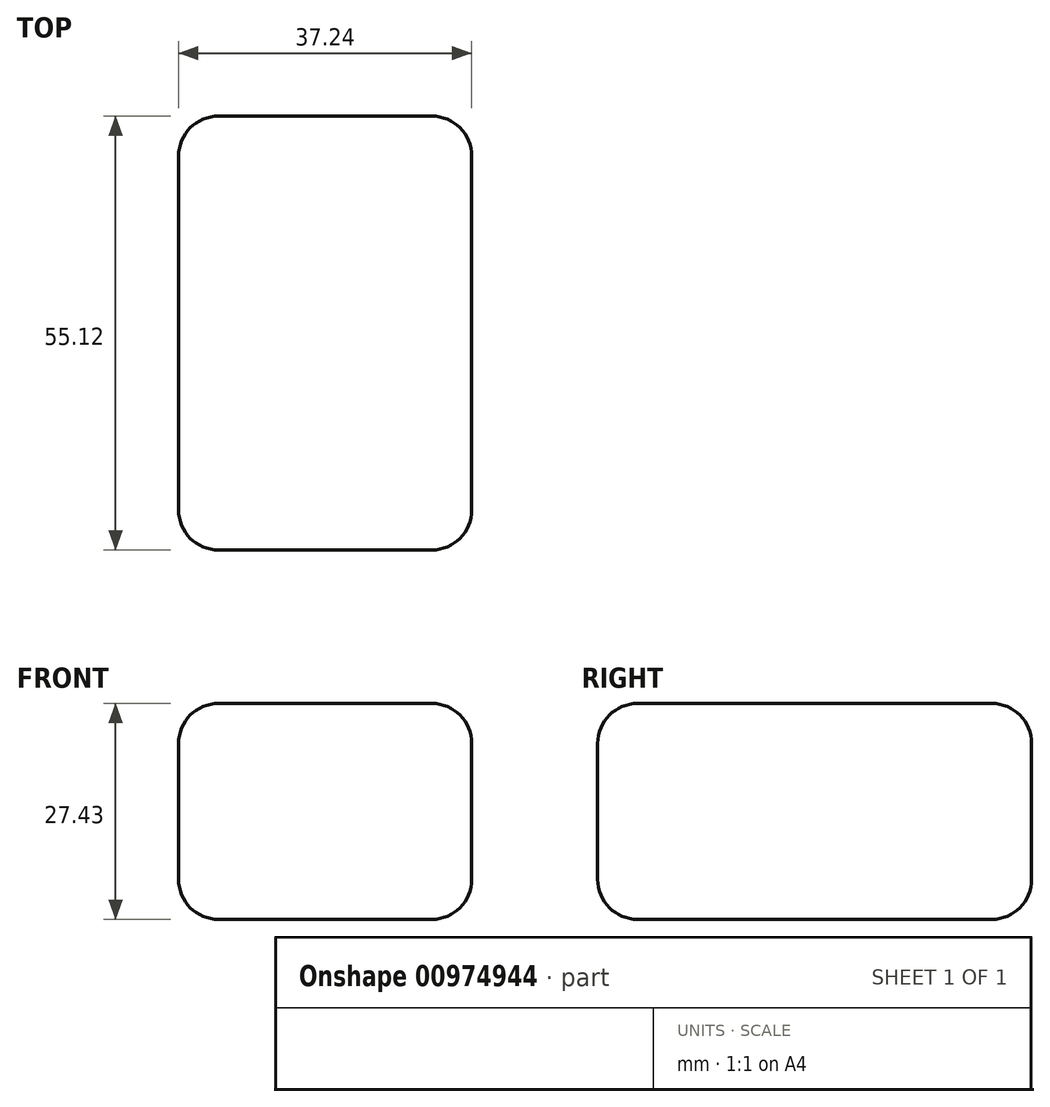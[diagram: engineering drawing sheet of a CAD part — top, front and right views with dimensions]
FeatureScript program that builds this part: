
annotation { "Feature Type Name" : "Feature", "Feature Type Description" : "" }
export const myFeature = defineFeature(function(context is Context, id is Id, definition is map)
    precondition{}
    {
        {
            var Q0;
            Q0=qCreatedBy(makeId("Top.planeOp"),FACE);
            var sketch = newSketch(context, id + "F0", { "sketchPlane" : qUnion([Q0])});
            skLineSegment(sketch, "E0.bottom", {"start": v(-67.38, 58.35) * mm, "end": v(-30.14, 58.35) * mm});
            skLineSegment(sketch, "E0.top", {"start": v(-67.38, 3.23) * mm, "end": v(-30.14, 3.23) * mm});
            skLineSegment(sketch, "E0.left", {"start": v(-67.38, 58.35) * mm, "end": v(-67.38, 3.23) * mm});
            skLineSegment(sketch, "E0.right", {"start": v(-30.14, 58.35) * mm, "end": v(-30.14, 3.23) * mm});
            skSolve(sketch);
        }
        {
            var Q0;
            Q0 = qSketchRegion(id + "F0", true);
            extrude(context, id + "F1", {"entities" : qUnion([Q0]), "depth" : 27.43 * mm, "offsetDistance" : 25.4 * mm});
        }
        {
            var Q0;
            Q0=makeQuery(id+"F1.opExtrude","CAP_EDGE",EDGE,{"disambiguationData":[OSD([sQuery(id+"F0.wireOp",EDGE,"E0.left")])],"isStart":false});
            var Q1;
            Q1=makeQuery(id+"F1.opExtrude","CAP_EDGE",EDGE,{"disambiguationData":[OSD([sQuery(id+"F0.wireOp",EDGE,"E0.right")])],"isStart":false});
            var Q2;
            Q2=makeQuery(id+"F1.opExtrude","CAP_EDGE",EDGE,{"disambiguationData":[OSD([sQuery(id+"F0.wireOp",EDGE,"E0.top")])],"isStart":false});
            var Q3;
            Q3=makeQuery(id+"F1.opExtrude","CAP_EDGE",EDGE,{"disambiguationData":[OSD([sQuery(id+"F0.wireOp",EDGE,"E0.bottom")])],"isStart":false});
            var Q4;
            Q4=makeQuery(id+"F1.opExtrude","CAP_EDGE",EDGE,{"disambiguationData":[OSD([sQuery(id+"F0.wireOp",EDGE,"E0.left")])],"isStart":true});
            var Q5;
            Q5=makeQuery(id+"F1.opExtrude","SWEPT_EDGE",EDGE,{"disambiguationData":[OSD([sQuery(id+"F0.wireOp",EDGE,"E0.bottom"),sQuery(id+"F0.wireOp",EDGE,"E0.left")])]});
            var Q6;
            Q6=makeQuery(id+"F1.opExtrude","SWEPT_EDGE",EDGE,{"disambiguationData":[OSD([sQuery(id+"F0.wireOp",EDGE,"E0.bottom"),sQuery(id+"F0.wireOp",EDGE,"E0.right")])]});
            var Q7;
            Q7=makeQuery(id+"F1.opExtrude","CAP_EDGE",EDGE,{"disambiguationData":[OSD([sQuery(id+"F0.wireOp",EDGE,"E0.bottom")])],"isStart":true});
            var Q8;
            Q8=makeQuery(id+"F1.opExtrude","SWEPT_EDGE",EDGE,{"disambiguationData":[OSD([sQuery(id+"F0.wireOp",EDGE,"E0.top"),sQuery(id+"F0.wireOp",EDGE,"E0.left")])]});
            var Q9;
            Q9=makeQuery(id+"F1.opExtrude","SWEPT_EDGE",EDGE,{"disambiguationData":[OSD([sQuery(id+"F0.wireOp",EDGE,"E0.top"),sQuery(id+"F0.wireOp",EDGE,"E0.right")])]});
            var Q10;
            Q10=makeQuery(id+"F1.opExtrude","CAP_EDGE",EDGE,{"disambiguationData":[OSD([sQuery(id+"F0.wireOp",EDGE,"E0.top")])],"isStart":true});
            var Q11;
            Q11=makeQuery(id+"F1.opExtrude","CAP_EDGE",EDGE,{"disambiguationData":[OSD([sQuery(id+"F0.wireOp",EDGE,"E0.right")])],"isStart":true});
            fillet(context, id + "F2", {"entities" : qUnion([Q0, Q1, Q2, Q3, Q4, Q5, Q6, Q7, Q8, Q9, Q10, Q11]), "tangentPropagation" : true, "radius" : 5.08 * mm, "defaultsChanged" : false, "vertexSettings" : [], "allowEdgeOverflow" : false});
        }
    });
